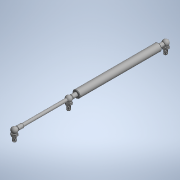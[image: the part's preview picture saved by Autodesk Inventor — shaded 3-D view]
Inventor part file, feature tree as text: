
AUTODESK INVENTOR PART (.ipt)
format: ipt  version: 2020 (Build 240168000, 168)  size: 1,027,072 bytes
history: native  units: mm (DEFAULTED — no unit token found)
features: boolean_combine x4, other x2, fillet x1
ambient origin geometry x8: Origin, YZ Plane, XZ Plane, XY Plane, X Axis, Y Axis, Z Axis, Center Point
bodies: Solid1 (feature_tree), Solid2 (feature_tree), Solid3 (feature_tree), Solid4 (feature_tree), Solid5 (feature_tree), Solid6 (feature_tree), Solid7 (feature_tree)
feature tree (7):
  other  "Cut-Revolve1"
  boolean_combine  "Combine1"
  boolean_combine  "Combine2"
  fillet  "Fillet1"  [1 undecoded]
  other  "LPattern1[1]"
  boolean_combine  "Combine7"
  boolean_combine  "Combine8"
note: 1 required parameter value undecoded (feature->parameter linkage not recoverable at this tier; creation-order binding heuristic only, values carry confidence <= 0.55)
